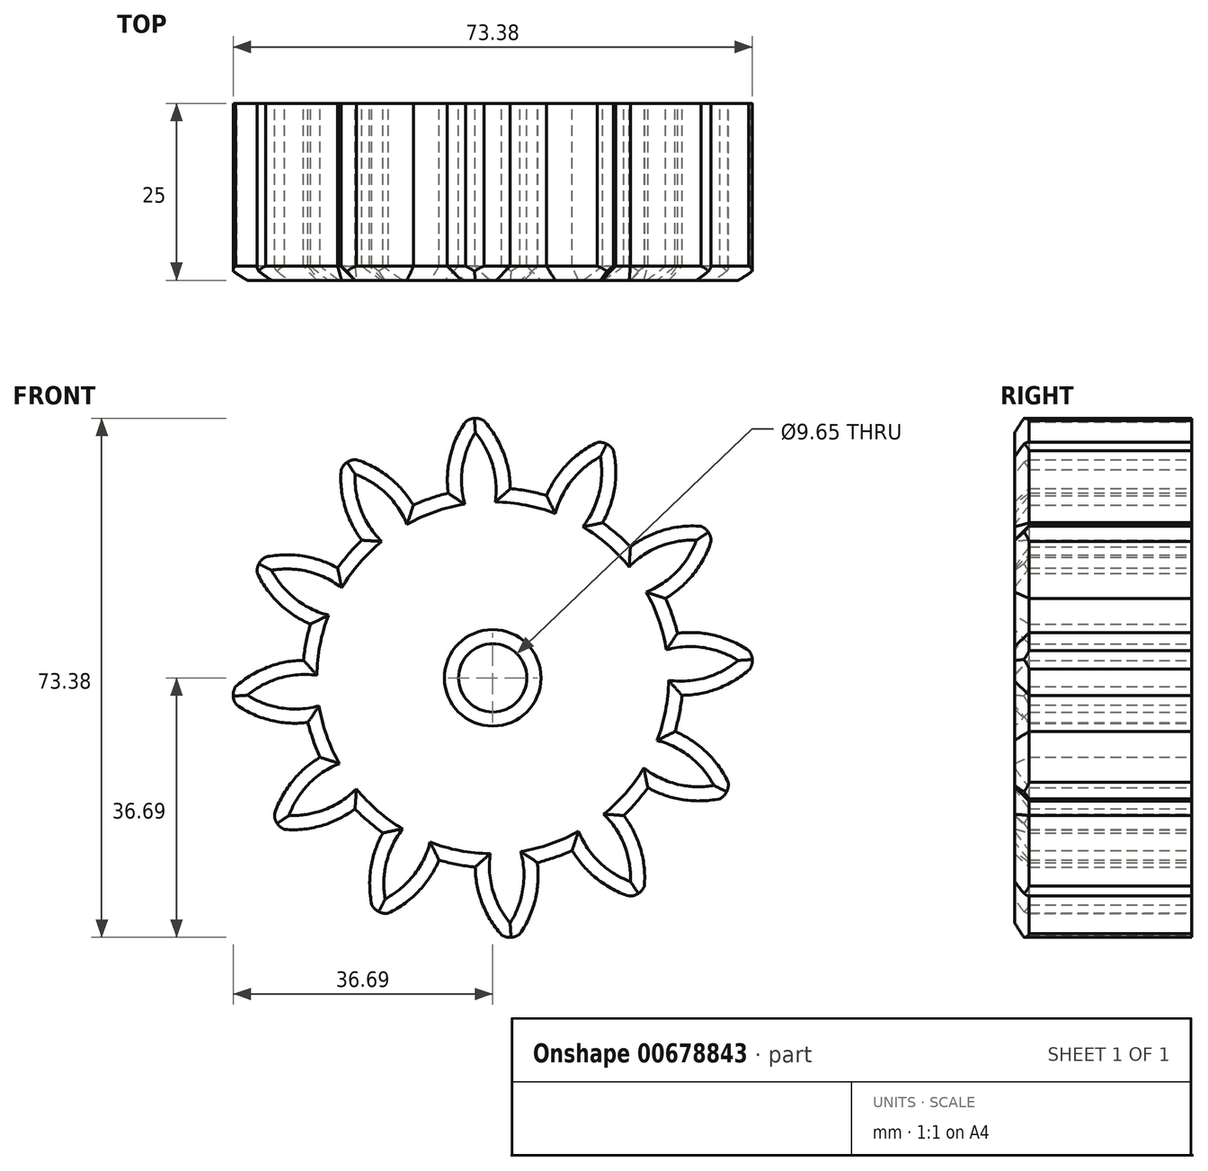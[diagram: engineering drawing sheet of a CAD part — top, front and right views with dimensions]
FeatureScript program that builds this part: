
annotation { "Feature Type Name" : "Feature", "Feature Type Description" : "" }
export const myFeature = defineFeature(function(context is Context, id is Id, definition is map)
    precondition{}
    {
        {
            var Q0;
            Q0=qCreatedBy(makeId("Front.planeOp"),FACE);
            var sketch = newSketch(context, id + "F0", { "sketchPlane" : qUnion([Q0])});
            skCircle(sketch, "E0", {"center": v(0, 0) * mm, "radius": 26.86 * mm});
            skCircle(sketch, "E1", {"center": v(0, 0) * mm, "radius": 29.36 * mm, "construction": true});
            skCircle(sketch, "E2", {"center": v(0, 0) * mm, "radius": 31.75 * mm, "construction": true});
            skLineSegment(sketch, "E3", {"start": v(0, 0) * mm, "end": v(0, 75.2) * mm, "construction": true});
            skLineSegment(sketch, "E4", {"start": v(0, 0) * mm, "end": v(-5.34, 81.5) * mm, "construction": true});
            skLineSegment(sketch, "E5", {"start": v(0, 29.36) * mm, "end": v(-72.87, 29.36) * mm, "construction": true});
            skLineSegment(sketch, "E6", {"start": v(0, 29.36) * mm, "end": v(-71.24, 3.43) * mm, "construction": true});
            skCircle(sketch, "E7", {"center": v(0, 0) * mm, "radius": 27.6 * mm, "construction": true});
            skCircle(sketch, "E8", {"center": v(0, 29.36) * mm, "radius": 14.6 * mm, "construction": true});
            skCircle(sketch, "E9", {"center": v(-13.72, 24.37) * mm, "radius": 14.6 * mm, "construction": true});
            skArc(sketch, "E10", {"start": v(1.6, 31.6) * mm, "mid": v(0.4, 34.1) * mm, "end": v(-1.26, 36.35) * mm});
            skArc(sketch, "E11", {"start": v(2.47, 26.63) * mm, "mid": v(2.25, 29.15) * mm, "end": v(1.6, 31.6) * mm});
            skArc(sketch, "E12.MirrorCS", {"start": v(-6.3, 26.06) * mm, "mid": v(-6.4, 28.58) * mm, "end": v(-6.07, 31.1) * mm});
            skArc(sketch, "E13.MirrorCS", {"start": v(-6.07, 31.1) * mm, "mid": v(-5.2, 33.74) * mm, "end": v(-3.86, 36.18) * mm});
            skArc(sketch, "E14", {"start": v(-1.26, 36.35) * mm, "mid": v(-2.59, 36.68) * mm, "end": v(-3.86, 36.18) * mm});
            skPoint(sketch, "E15.0.midPoint", {"position": v(-4.84, 5.45) * mm});
            skCircle(sketch, "E16", {"center": v(0, 0) * mm, "radius": 4.82 * mm});
            skSolve(sketch);
        }
        {
            var Q0;
            Q0=makeQuery(id+"F0.imprint","IMPRINT",FACE,{"disambiguationData":[TD([[makeQuery(id+"F0.imprint","IMPRINT",EDGE,{"derivedFrom":sQuery(id+"F0.wireOp",EDGE,"E0")}),1.0]])]});
            var Q1;
            {var subQ5=sQuery(id+"F0.wireOp",EDGE,"E10");Q1=makeQuery(id+"F0.imprint","IMPRINT",FACE,{"disambiguationData":[TD([[makeQuery(id+"F0.imprint","IMPRINT",EDGE,{"derivedFrom":subQ5}),1.0]])]});}
            extrude(context, id + "F1", {"entities" : qUnion([Q0, Q1]), "depth" : 25 * mm, "offsetDistance" : 25 * mm});
        }
        {
            var Q0;
            Q0=makeQuery(id+"F1.opExtrude","SWEPT_BODY",BODY,{"disambiguationData":[OSD([sQuery(id+"F0.wireOp",EDGE,"E0"),sQuery(id+"F0.wireOp",EDGE,"ydpJjS2L-kiQ3-pLyA-xjUn-Sw7KcbjrEqpt"),sQuery(id+"F0.wireOp",EDGE,"FveCbRr8-ogRx-ZfIS-3U2Q-XbR6Kket0EV6"),sQuery(id+"F0.wireOp",EDGE,"4ebee775-e82f-48df-9f5d-394f6b318d0d0.MirrorCS"),sQuery(id+"F0.wireOp",EDGE,"75975aa6-e8ec-4230-81f9-42a67bc54c7b0.MirrorCS"),sQuery(id+"F0.wireOp",EDGE,"01Of4uWr-96tw-7Odv-lFzN-XObHPhth0YCY")])]});
            var Q1;
            Q1=makeQuery(id+"F1.opExtrude","SWEPT_FACE",FACE,{"disambiguationData":[OSD([sQuery(id+"F0.wireOp",EDGE,"E0")])]});
            circularPattern(context, id + "F2", {"operationType" : NewBodyOperationType.ADD, "entities" : qUnion([Q0]), "axis" : qUnion([Q1]), "angle" : 360 * degree, "instanceCount" : 12, "equalSpace" : true});
        }
        {
            var Q0;
            Q0=makeQuery(id+"F2.opPattern","COPY",EDGE,{"derivedFrom":makeQuery(id+"F1.opExtrude","CAP_EDGE",EDGE,{"disambiguationData":[OSD([sQuery(id+"F0.wireOp",EDGE,"01Of4uWr-96tw-7Odv-lFzN-XObHPhth0YCY")])],"isStart":false}),"instanceName":"21"});
            var Q1;
            Q1=makeQuery(id+"F2.opPattern","COPY",EDGE,{"derivedFrom":makeQuery(id+"F1.opExtrude","CAP_EDGE",EDGE,{"disambiguationData":[OSD([sQuery(id+"F0.wireOp",EDGE,"ydpJjS2L-kiQ3-pLyA-xjUn-Sw7KcbjrEqpt")])],"isStart":false}),"instanceName":"21"});
            var Q2;
            Q2=makeQuery(id+"F2.opPattern","COPY",EDGE,{"derivedFrom":makeQuery(id+"F1.opExtrude","CAP_EDGE",EDGE,{"disambiguationData":[OSD([sQuery(id+"F0.wireOp",EDGE,"FveCbRr8-ogRx-ZfIS-3U2Q-XbR6Kket0EV6")])],"isStart":false}),"instanceName":"21"});
            var Q3;
            Q3=makeQuery(id+"F2.opPattern","COPY",EDGE,{"derivedFrom":makeQuery(id+"F1.opExtrude","CAP_EDGE",EDGE,{"disambiguationData":[OSD([sQuery(id+"F0.wireOp",EDGE,"75975aa6-e8ec-4230-81f9-42a67bc54c7b0.MirrorCS")])],"isStart":false}),"instanceName":"21"});
            var Q4;
            Q4=makeQuery(id+"F2.opPattern","COPY",EDGE,{"derivedFrom":makeQuery(id+"F1.opExtrude","CAP_EDGE",EDGE,{"disambiguationData":[OSD([sQuery(id+"F0.wireOp",EDGE,"4ebee775-e82f-48df-9f5d-394f6b318d0d0.MirrorCS")])],"isStart":false}),"instanceName":"21"});
            var Q5;
            Q5=makeQuery(id+"F1.opExtrude","CAP_EDGE",EDGE,{"disambiguationData":[OSD([sQuery(id+"F0.wireOp",EDGE,"01Of4uWr-96tw-7Odv-lFzN-XObHPhth0YCY")])],"isStart":false});
            var Q6;
            Q6=makeQuery(id+"F1.opExtrude","CAP_EDGE",EDGE,{"disambiguationData":[OSD([sQuery(id+"F0.wireOp",EDGE,"75975aa6-e8ec-4230-81f9-42a67bc54c7b0.MirrorCS")])],"isStart":false});
            var Q7;
            Q7=makeQuery(id+"F1.opExtrude","CAP_EDGE",EDGE,{"disambiguationData":[OSD([sQuery(id+"F0.wireOp",EDGE,"ydpJjS2L-kiQ3-pLyA-xjUn-Sw7KcbjrEqpt")])],"isStart":false});
            var Q8;
            Q8=makeQuery(id+"F1.opExtrude","CAP_EDGE",EDGE,{"disambiguationData":[OSD([sQuery(id+"F0.wireOp",EDGE,"4ebee775-e82f-48df-9f5d-394f6b318d0d0.MirrorCS")])],"isStart":false});
            var Q9;
            Q9=makeQuery(id+"F1.opExtrude","CAP_EDGE",EDGE,{"disambiguationData":[OSD([sQuery(id+"F0.wireOp",EDGE,"FveCbRr8-ogRx-ZfIS-3U2Q-XbR6Kket0EV6")])],"isStart":false});
            var Q10;
            Q10=makeQuery(id+"F2.opPattern","COPY",EDGE,{"derivedFrom":makeQuery(id+"F1.opExtrude","CAP_EDGE",EDGE,{"disambiguationData":[OSD([sQuery(id+"F0.wireOp",EDGE,"75975aa6-e8ec-4230-81f9-42a67bc54c7b0.MirrorCS")])],"isStart":false}),"instanceName":"22"});
            var Q11;
            Q11=makeQuery(id+"F2.opPattern","COPY",EDGE,{"derivedFrom":makeQuery(id+"F1.opExtrude","CAP_EDGE",EDGE,{"disambiguationData":[OSD([sQuery(id+"F0.wireOp",EDGE,"01Of4uWr-96tw-7Odv-lFzN-XObHPhth0YCY")])],"isStart":false}),"instanceName":"22"});
            var Q12;
            Q12=makeQuery(id+"F2.opPattern","COPY",EDGE,{"derivedFrom":makeQuery(id+"F1.opExtrude","CAP_EDGE",EDGE,{"disambiguationData":[OSD([sQuery(id+"F0.wireOp",EDGE,"4ebee775-e82f-48df-9f5d-394f6b318d0d0.MirrorCS")])],"isStart":false}),"instanceName":"22"});
            var Q13;
            Q13=makeQuery(id+"F2.opPattern","COPY",EDGE,{"derivedFrom":makeQuery(id+"F1.opExtrude","CAP_EDGE",EDGE,{"disambiguationData":[OSD([sQuery(id+"F0.wireOp",EDGE,"ydpJjS2L-kiQ3-pLyA-xjUn-Sw7KcbjrEqpt")])],"isStart":false}),"instanceName":"22"});
            var Q14;
            Q14=makeQuery(id+"F2.opPattern","COPY",EDGE,{"derivedFrom":makeQuery(id+"F1.opExtrude","CAP_EDGE",EDGE,{"disambiguationData":[OSD([sQuery(id+"F0.wireOp",EDGE,"FveCbRr8-ogRx-ZfIS-3U2Q-XbR6Kket0EV6")])],"isStart":false}),"instanceName":"22"});
            var Q15;
            Q15=makeQuery(id+"F2.opPattern","COPY",EDGE,{"derivedFrom":makeQuery(id+"F1.opExtrude","CAP_EDGE",EDGE,{"disambiguationData":[OSD([sQuery(id+"F0.wireOp",EDGE,"75975aa6-e8ec-4230-81f9-42a67bc54c7b0.MirrorCS")])],"isStart":false}),"instanceName":"23"});
            var Q16;
            Q16=makeQuery(id+"F2.opPattern","COPY",EDGE,{"derivedFrom":makeQuery(id+"F1.opExtrude","CAP_EDGE",EDGE,{"disambiguationData":[OSD([sQuery(id+"F0.wireOp",EDGE,"01Of4uWr-96tw-7Odv-lFzN-XObHPhth0YCY")])],"isStart":false}),"instanceName":"23"});
            var Q17;
            Q17=makeQuery(id+"F2.opPattern","COPY",EDGE,{"derivedFrom":makeQuery(id+"F1.opExtrude","CAP_EDGE",EDGE,{"disambiguationData":[OSD([sQuery(id+"F0.wireOp",EDGE,"ydpJjS2L-kiQ3-pLyA-xjUn-Sw7KcbjrEqpt")])],"isStart":false}),"instanceName":"23"});
            var Q18;
            Q18=makeQuery(id+"F2.opPattern","COPY",EDGE,{"derivedFrom":makeQuery(id+"F1.opExtrude","CAP_EDGE",EDGE,{"disambiguationData":[OSD([sQuery(id+"F0.wireOp",EDGE,"FveCbRr8-ogRx-ZfIS-3U2Q-XbR6Kket0EV6")])],"isStart":false}),"instanceName":"23"});
            var Q19;
            Q19=makeQuery(id+"F2.opPattern","COPY",EDGE,{"derivedFrom":makeQuery(id+"F1.opExtrude","CAP_EDGE",EDGE,{"disambiguationData":[OSD([sQuery(id+"F0.wireOp",EDGE,"4ebee775-e82f-48df-9f5d-394f6b318d0d0.MirrorCS")])],"isStart":false}),"instanceName":"23"});
            var Q20;
            Q20=makeQuery(id+"F2.opPattern","COPY",EDGE,{"derivedFrom":makeQuery(id+"F1.opExtrude","CAP_EDGE",EDGE,{"disambiguationData":[OSD([sQuery(id+"F0.wireOp",EDGE,"01Of4uWr-96tw-7Odv-lFzN-XObHPhth0YCY")])],"isStart":false}),"instanceName":"20"});
            var Q21;
            Q21=makeQuery(id+"F2.opPattern","COPY",EDGE,{"derivedFrom":makeQuery(id+"F1.opExtrude","CAP_EDGE",EDGE,{"disambiguationData":[OSD([sQuery(id+"F0.wireOp",EDGE,"ydpJjS2L-kiQ3-pLyA-xjUn-Sw7KcbjrEqpt")])],"isStart":false}),"instanceName":"20"});
            var Q22;
            Q22=makeQuery(id+"F2.opPattern","COPY",EDGE,{"derivedFrom":makeQuery(id+"F1.opExtrude","CAP_EDGE",EDGE,{"disambiguationData":[OSD([sQuery(id+"F0.wireOp",EDGE,"FveCbRr8-ogRx-ZfIS-3U2Q-XbR6Kket0EV6")])],"isStart":false}),"instanceName":"20"});
            var Q23;
            Q23=makeQuery(id+"F2.opPattern","COPY",EDGE,{"derivedFrom":makeQuery(id+"F1.opExtrude","CAP_EDGE",EDGE,{"disambiguationData":[OSD([sQuery(id+"F0.wireOp",EDGE,"75975aa6-e8ec-4230-81f9-42a67bc54c7b0.MirrorCS")])],"isStart":false}),"instanceName":"20"});
            var Q24;
            Q24=makeQuery(id+"F2.opPattern","COPY",EDGE,{"derivedFrom":makeQuery(id+"F1.opExtrude","CAP_EDGE",EDGE,{"disambiguationData":[OSD([sQuery(id+"F0.wireOp",EDGE,"4ebee775-e82f-48df-9f5d-394f6b318d0d0.MirrorCS")])],"isStart":false}),"instanceName":"20"});
            var Q25;
            Q25=makeQuery(id+"F2.opPattern","COPY",EDGE,{"derivedFrom":makeQuery(id+"F1.opExtrude","CAP_EDGE",EDGE,{"disambiguationData":[OSD([sQuery(id+"F0.wireOp",EDGE,"ydpJjS2L-kiQ3-pLyA-xjUn-Sw7KcbjrEqpt")])],"isStart":false}),"instanceName":"19"});
            var Q26;
            Q26=makeQuery(id+"F2.opPattern","COPY",EDGE,{"derivedFrom":makeQuery(id+"F1.opExtrude","CAP_EDGE",EDGE,{"disambiguationData":[OSD([sQuery(id+"F0.wireOp",EDGE,"FveCbRr8-ogRx-ZfIS-3U2Q-XbR6Kket0EV6")])],"isStart":false}),"instanceName":"19"});
            var Q27;
            Q27=makeQuery(id+"F2.opPattern","COPY",EDGE,{"derivedFrom":makeQuery(id+"F1.opExtrude","CAP_EDGE",EDGE,{"disambiguationData":[OSD([sQuery(id+"F0.wireOp",EDGE,"01Of4uWr-96tw-7Odv-lFzN-XObHPhth0YCY")])],"isStart":false}),"instanceName":"19"});
            var Q28;
            Q28=makeQuery(id+"F2.opPattern","COPY",EDGE,{"derivedFrom":makeQuery(id+"F1.opExtrude","CAP_EDGE",EDGE,{"disambiguationData":[OSD([sQuery(id+"F0.wireOp",EDGE,"75975aa6-e8ec-4230-81f9-42a67bc54c7b0.MirrorCS")])],"isStart":false}),"instanceName":"19"});
            var Q29;
            Q29=makeQuery(id+"F2.opPattern","COPY",EDGE,{"derivedFrom":makeQuery(id+"F1.opExtrude","CAP_EDGE",EDGE,{"disambiguationData":[OSD([sQuery(id+"F0.wireOp",EDGE,"4ebee775-e82f-48df-9f5d-394f6b318d0d0.MirrorCS")])],"isStart":false}),"instanceName":"19"});
            var Q30;
            Q30=makeQuery(id+"F2.opPattern","COPY",EDGE,{"derivedFrom":makeQuery(id+"F1.opExtrude","CAP_EDGE",EDGE,{"disambiguationData":[OSD([sQuery(id+"F0.wireOp",EDGE,"01Of4uWr-96tw-7Odv-lFzN-XObHPhth0YCY")])],"isStart":false}),"instanceName":"18"});
            var Q31;
            Q31=makeQuery(id+"F2.opPattern","COPY",EDGE,{"derivedFrom":makeQuery(id+"F1.opExtrude","CAP_EDGE",EDGE,{"disambiguationData":[OSD([sQuery(id+"F0.wireOp",EDGE,"75975aa6-e8ec-4230-81f9-42a67bc54c7b0.MirrorCS")])],"isStart":false}),"instanceName":"18"});
            var Q32;
            Q32=makeQuery(id+"F2.opPattern","COPY",EDGE,{"derivedFrom":makeQuery(id+"F1.opExtrude","CAP_EDGE",EDGE,{"disambiguationData":[OSD([sQuery(id+"F0.wireOp",EDGE,"4ebee775-e82f-48df-9f5d-394f6b318d0d0.MirrorCS")])],"isStart":false}),"instanceName":"18"});
            var Q33;
            Q33=makeQuery(id+"F2.opPattern","COPY",EDGE,{"derivedFrom":makeQuery(id+"F1.opExtrude","CAP_EDGE",EDGE,{"disambiguationData":[OSD([sQuery(id+"F0.wireOp",EDGE,"ydpJjS2L-kiQ3-pLyA-xjUn-Sw7KcbjrEqpt")])],"isStart":false}),"instanceName":"18"});
            var Q34;
            {var subQ0=makeQuery(id+"F1.opExtrude","CAP_FACE",FACE,{"disambiguationData":[OSD([sQuery(id+"F0.wireOp",EDGE,"E0"),sQuery(id+"F0.wireOp",EDGE,"ydpJjS2L-kiQ3-pLyA-xjUn-Sw7KcbjrEqpt"),sQuery(id+"F0.wireOp",EDGE,"FveCbRr8-ogRx-ZfIS-3U2Q-XbR6Kket0EV6"),sQuery(id+"F0.wireOp",EDGE,"4ebee775-e82f-48df-9f5d-394f6b318d0d0.MirrorCS"),sQuery(id+"F0.wireOp",EDGE,"75975aa6-e8ec-4230-81f9-42a67bc54c7b0.MirrorCS"),sQuery(id+"F0.wireOp",EDGE,"01Of4uWr-96tw-7Odv-lFzN-XObHPhth0YCY"),sQuery(id+"F0.wireOp",EDGE,"hntcVUhS-Lo8d-CZzQ-hoLm-zFAirhotr0I7")])],"isStart":false});Q34=makeQuery(id+"F6ieS007t5YNEpl_1.boolean.opBoolean","MERGE",FACE,{"derivedFrom":[subQ0,makeQuery(id+"F2.opPattern","COPY",FACE,{"derivedFrom":subQ0,"instanceName":"1"}),makeQuery(id+"F2.opPattern","COPY",FACE,{"derivedFrom":subQ0,"instanceName":"2"}),makeQuery(id+"F2.opPattern","COPY",FACE,{"derivedFrom":subQ0,"instanceName":"3"}),makeQuery(id+"F2.opPattern","COPY",FACE,{"derivedFrom":subQ0,"instanceName":"4"}),makeQuery(id+"F2.opPattern","COPY",FACE,{"derivedFrom":subQ0,"instanceName":"5"}),makeQuery(id+"F2.opPattern","COPY",FACE,{"derivedFrom":subQ0,"instanceName":"6"}),makeQuery(id+"F2.opPattern","COPY",FACE,{"derivedFrom":subQ0,"instanceName":"7"}),makeQuery(id+"F2.opPattern","COPY",FACE,{"derivedFrom":subQ0,"instanceName":"8"}),makeQuery(id+"F2.opPattern","COPY",FACE,{"derivedFrom":subQ0,"instanceName":"9"}),makeQuery(id+"F2.opPattern","COPY",FACE,{"derivedFrom":subQ0,"instanceName":"10"}),makeQuery(id+"F2.opPattern","COPY",FACE,{"derivedFrom":subQ0,"instanceName":"11"}),makeQuery(id+"F2.opPattern","COPY",FACE,{"derivedFrom":subQ0,"instanceName":"12"}),makeQuery(id+"F2.opPattern","COPY",FACE,{"derivedFrom":subQ0,"instanceName":"13"}),makeQuery(id+"F2.opPattern","COPY",FACE,{"derivedFrom":subQ0,"instanceName":"14"}),makeQuery(id+"F2.opPattern","COPY",FACE,{"derivedFrom":subQ0,"instanceName":"15"}),makeQuery(id+"F2.opPattern","COPY",FACE,{"derivedFrom":subQ0,"instanceName":"16"}),makeQuery(id+"F2.opPattern","COPY",FACE,{"derivedFrom":subQ0,"instanceName":"17"}),makeQuery(id+"F2.opPattern","COPY",FACE,{"derivedFrom":subQ0,"instanceName":"18"}),makeQuery(id+"F2.opPattern","COPY",FACE,{"derivedFrom":subQ0,"instanceName":"19"}),makeQuery(id+"F2.opPattern","COPY",FACE,{"derivedFrom":subQ0,"instanceName":"20"}),makeQuery(id+"F2.opPattern","COPY",FACE,{"derivedFrom":subQ0,"instanceName":"21"}),makeQuery(id+"F2.opPattern","COPY",FACE,{"derivedFrom":subQ0,"instanceName":"22"}),makeQuery(id+"F2.opPattern","COPY",FACE,{"derivedFrom":subQ0,"instanceName":"23"})]});}
            chamfer(context, id + "F3", {"entities" : qUnion([Q0, Q1, Q2, Q3, Q4, Q5, Q6, Q7, Q8, Q9, Q10, Q11, Q12, Q13, Q14, Q15, Q16, Q17, Q18, Q19, Q20, Q21, Q22, Q23, Q24, Q25, Q26, Q27, Q28, Q29, Q30, Q31, Q32, Q33, Q34]), "width" : 2 * mm, "tangentPropagation" : true});
        }
    });
